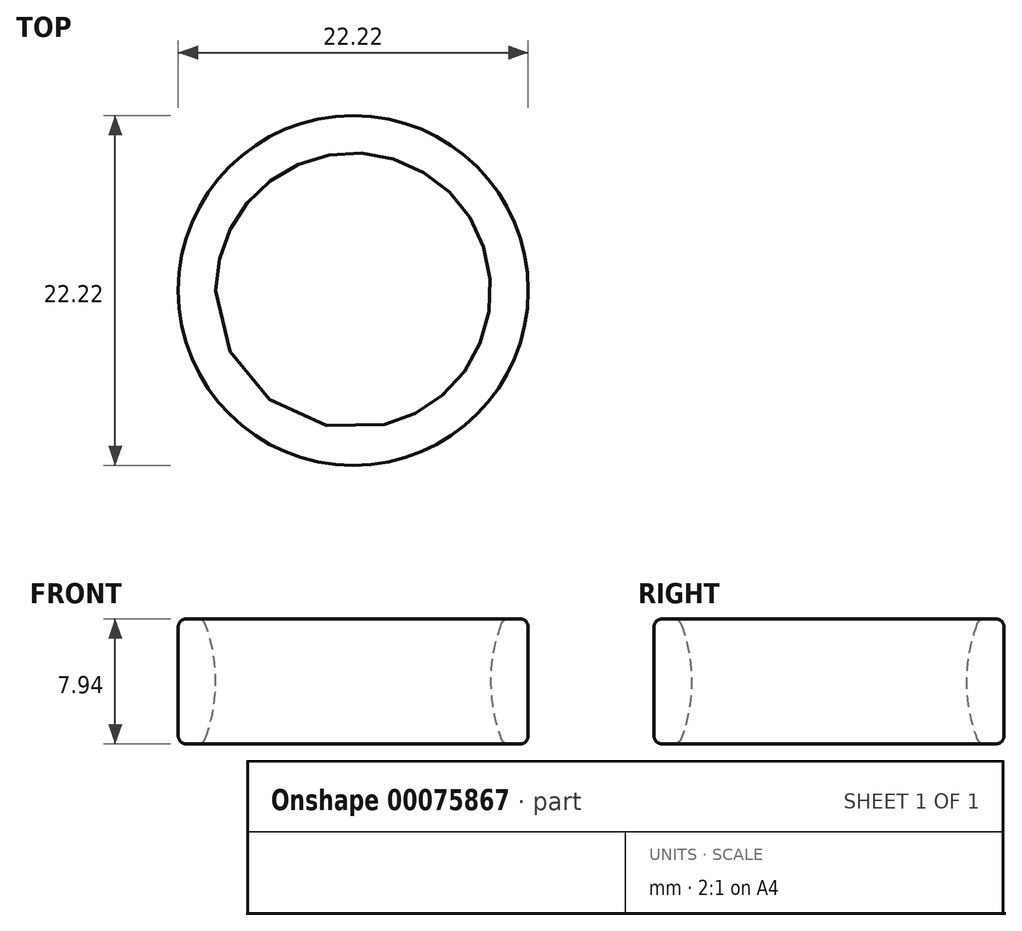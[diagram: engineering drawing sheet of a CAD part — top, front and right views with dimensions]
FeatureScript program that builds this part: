
annotation { "Feature Type Name" : "Feature", "Feature Type Description" : "" }
export const myFeature = defineFeature(function(context is Context, id is Id, definition is map)
    precondition{}
    {
        {
            var Q0;
            Q0=qCreatedBy(makeId("Front.planeOp"),FACE);
            var sketch = newSketch(context, id + "F0", { "sketchPlane" : qUnion([Q0])});
            skLineSegment(sketch, "E0", {"start": v(-9.87, 7.94) * mm, "end": v(-10.6, 7.94) * mm});
            skLineSegment(sketch, "E1", {"start": v(-11.11, 7.43) * mm, "end": v(-11.11, 0.5) * mm});
            skLineSegment(sketch, "E2", {"start": v(-10.6, 0) * mm, "end": v(-9.87, 0) * mm});
            skArc(sketch, "E3", {"start": v(-9.4, 0.33) * mm, "mid": v(-8.73, 3.97) * mm, "end": v(-9.4, 7.6) * mm});
            skLineSegment(sketch, "E4.MirrorCS", {"start": v(10.6, 0) * mm, "end": v(9.87, 0) * mm});
            skLineSegment(sketch, "E5.MirrorCS", {"start": v(9.87, 7.94) * mm, "end": v(10.6, 7.94) * mm});
            skLineSegment(sketch, "E6.MirrorCS", {"start": v(11.11, 7.43) * mm, "end": v(11.11, 0.5) * mm});
            skArc(sketch, "E7.MirrorCS", {"start": v(9.4, 0.33) * mm, "mid": v(8.73, 3.97) * mm, "end": v(9.4, 7.6) * mm});
            skPoint(sketch, "E8.visualSharp", {"position": v(-11.11, 7.94) * mm});
            skArc(sketch, "E8.filletArc", {"start": v(-10.6, 7.94) * mm, "mid": v(-10.96, 7.79) * mm, "end": v(-11.11, 7.43) * mm});
            skPoint(sketch, "E9.visualSharp", {"position": v(-9.53, 7.94) * mm});
            skArc(sketch, "E9.filletArc", {"start": v(-9.4, 7.6) * mm, "mid": v(-9.58, 7.85) * mm, "end": v(-9.87, 7.94) * mm});
            skPoint(sketch, "E10.visualSharp", {"position": v(-9.53, 0) * mm});
            skArc(sketch, "E10.filletArc", {"start": v(-9.87, 0) * mm, "mid": v(-9.58, 0.1) * mm, "end": v(-9.4, 0.33) * mm});
            skPoint(sketch, "E11.visualSharp", {"position": v(-11.11, 0) * mm});
            skArc(sketch, "E11.filletArc", {"start": v(-11.11, 0.5) * mm, "mid": v(-10.96, 0.15) * mm, "end": v(-10.6, 0) * mm});
            skPoint(sketch, "E12.visualSharp", {"position": v(9.53, 7.94) * mm});
            skArc(sketch, "E12.filletArc", {"start": v(9.87, 7.94) * mm, "mid": v(9.58, 7.85) * mm, "end": v(9.4, 7.6) * mm});
            skPoint(sketch, "E13.visualSharp", {"position": v(11.11, 7.94) * mm});
            skArc(sketch, "E13.filletArc", {"start": v(11.11, 7.43) * mm, "mid": v(10.96, 7.79) * mm, "end": v(10.6, 7.94) * mm});
            skPoint(sketch, "E14.visualSharp", {"position": v(11.11, 0) * mm});
            skArc(sketch, "E14.filletArc", {"start": v(10.6, 0) * mm, "mid": v(10.96, 0.15) * mm, "end": v(11.11, 0.5) * mm});
            skPoint(sketch, "E15.visualSharp", {"position": v(9.53, 0) * mm});
            skArc(sketch, "E15.filletArc", {"start": v(9.4, 0.33) * mm, "mid": v(9.58, 0.1) * mm, "end": v(9.87, 0) * mm});
            skLineSegment(sketch, "E16", {"start": v(0, 0) * mm, "end": v(0, 7.94) * mm, "construction": true});
            skSolve(sketch);
        }
        {
            var Q0;
            Q0=makeQuery(id+"F0.imprint","IMPRINT",FACE,{"disambiguationData":[TD([[makeQuery(id+"F0.imprint","IMPRINT",EDGE,{"derivedFrom":sQuery(id+"F0.wireOp",EDGE,"E0")}),1.0]])]});
            var Q1;
            Q1 = qConstructionFilter(qBodyType(qCreatedBy(id + "F0" ,EDGE), BodyType.WIRE), ConstructionObject.NO);
            var Q2;
            Q2=sQuery(id+"F0.wireOp",EDGE,"E16");
            revolve(context, id + "F1", {"entities" : qUnion([Q0]), "surfaceEntities" : qUnion([Q1]), "axis" : qUnion([Q2]), "revolveType" : RevolveType.FULL});
        }
    });
